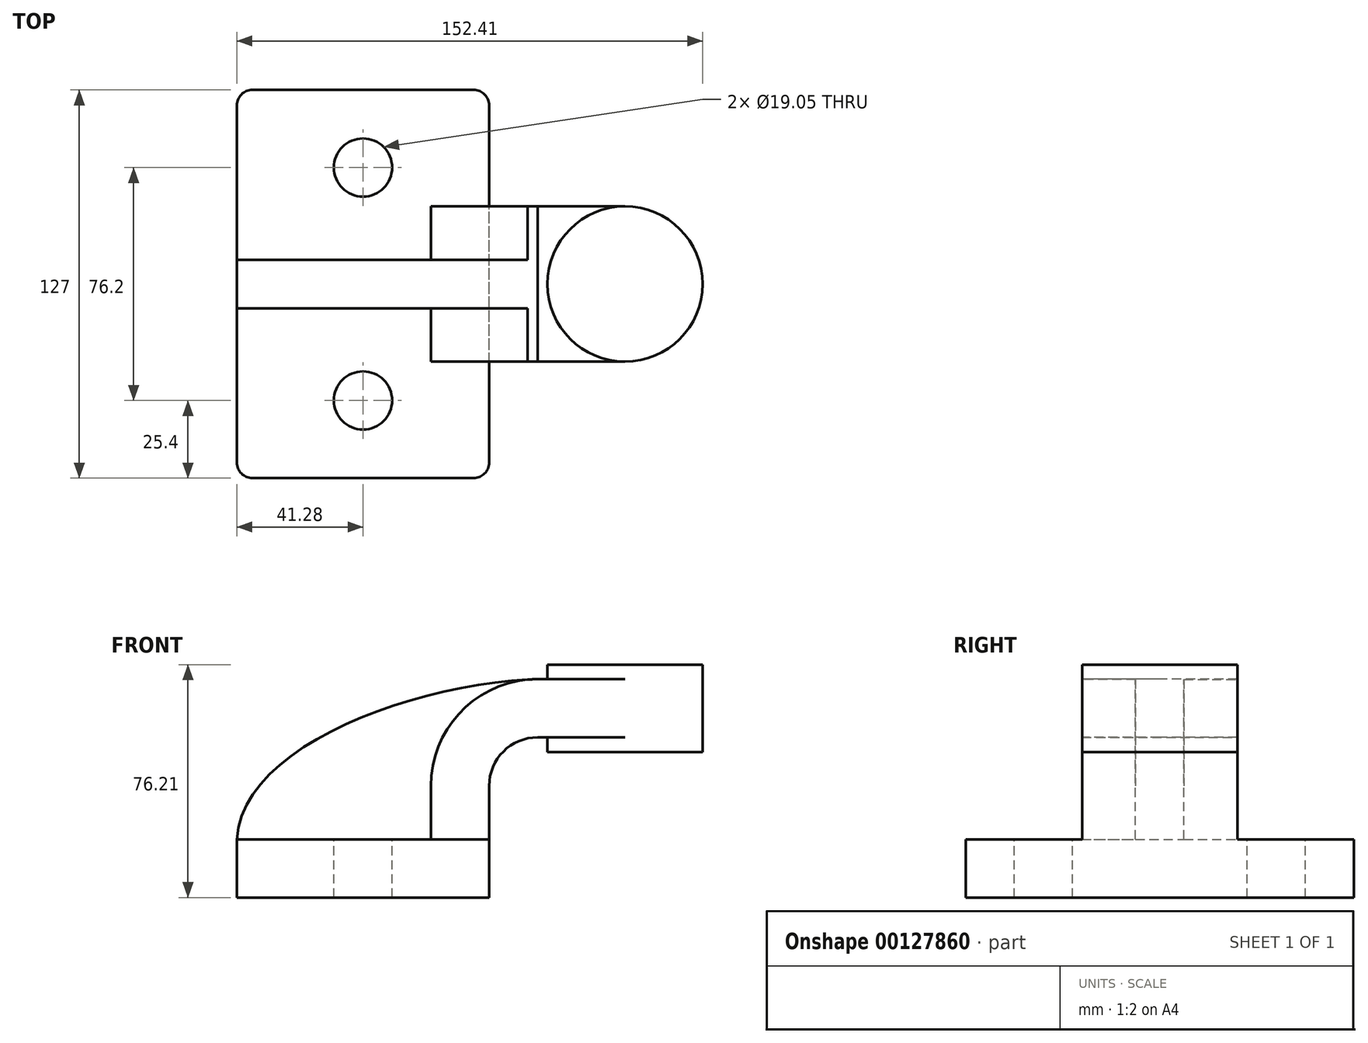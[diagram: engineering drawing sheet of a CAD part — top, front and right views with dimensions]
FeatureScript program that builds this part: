
annotation { "Feature Type Name" : "Feature", "Feature Type Description" : "" }
export const myFeature = defineFeature(function(context is Context, id is Id, definition is map)
    precondition{}
    {
        {
            var Q0;
            Q0=qCreatedBy(makeId("Front.planeOp"),FACE);
            var sketch = newSketch(context, id + "F0", { "sketchPlane" : qUnion([Q0])});
            skLineSegment(sketch, "E0.rect.bottom", {"start": v(-41.28, 9.52) * mm, "end": v(41.28, 9.52) * mm});
            skLineSegment(sketch, "E0.rect.top", {"start": v(-41.28, -9.52) * mm, "end": v(41.28, -9.52) * mm});
            skLineSegment(sketch, "E0.rect.left", {"start": v(-41.28, 9.52) * mm, "end": v(-41.28, -9.52) * mm});
            skLineSegment(sketch, "E0.rect.right", {"start": v(41.28, 9.52) * mm, "end": v(41.28, -9.52) * mm});
            skPoint(sketch, "E0.rect.middle", {"position": v(0, 0) * mm});
            skLineSegment(sketch, "E1", {"start": v(41.28, 9.52) * mm, "end": v(41.28, 27) * mm});
            skArc(sketch, "E2", {"start": v(41.28, 27) * mm, "mid": v(45.92, 38.23) * mm, "end": v(57.15, 42.88) * mm});
            skLineSegment(sketch, "E3", {"start": v(57.15, 42.88) * mm, "end": v(85.72, 42.88) * mm});
            skLineSegment(sketch, "E4.rect.bottom", {"start": v(60.32, 38.1) * mm, "end": v(111.12, 38.1) * mm});
            skLineSegment(sketch, "E4.rect.top", {"start": v(60.32, 66.68) * mm, "end": v(111.12, 66.68) * mm});
            skLineSegment(sketch, "E4.rect.left", {"start": v(60.32, 38.1) * mm, "end": v(60.32, 66.68) * mm});
            skLineSegment(sketch, "E4.rect.right", {"start": v(111.13, 38.1) * mm, "end": v(111.12, 66.68) * mm});
            skPoint(sketch, "E4.rect.middle", {"position": v(85.72, 52.39) * mm});
            skLineSegment(sketch, "E5.0", {"start": v(57.15, 61.93) * mm, "end": v(85.72, 61.93) * mm});
            skArc(sketch, "E5.1", {"start": v(22.23, 27) * mm, "mid": v(32.45, 51.7) * mm, "end": v(57.15, 61.93) * mm});
            skLineSegment(sketch, "E5.2", {"start": v(22.23, 9.52) * mm, "end": v(22.23, 27) * mm});
            skLineSegment(sketch, "E6", {"start": v(85.72, 38.1) * mm, "end": v(85.72, 66.68) * mm});
            skFitSpline(sketch, "E7", {"points": [v(-41.28, 9.53) * mm, v(57.15, 61.93) * mm], "startDerivative": vector(5.2, 92.34) * mm, "endDerivative": vector(120.92, 4.22) * mm});
            skSolve(sketch);
        }
        {
            var Q0;
            Q0=makeQuery(id+"F0.imprint","IMPRINT",FACE,{"disambiguationData":[TD([[makeQuery(id+"F0.imprint","IMPRINT",EDGE,{"derivedFrom":sQuery(id+"F0.wireOp",EDGE,"E0.rect.top")}),1.0]])]});
            extrude(context, id + "F1", {"entities" : qUnion([Q0]), "endBound" : BoundingType.SYMMETRIC, "depth" : 127 * mm});
        }
        {
            var Q0;
            {var subQ9=sQuery(id+"F0.wireOp",EDGE,"E1");Q0=makeQuery(id+"F0.imprint","IMPRINT",FACE,{"disambiguationData":[TD([[makeQuery(id+"F0.imprint","IMPRINT",EDGE,{"derivedFrom":subQ9}),1.0]])]});}
            var Q1;
            {var subQ0=sQuery(id+"F0.wireOp",EDGE,"E6");var subQ1=sQuery(id+"F0.wireOp",EDGE,"E3");var subQ2=makeQuery(id+"F0.imprint","INTERSECT",VERTEX,{"derivedFrom":[subQ1,subQ0]});Q1=makeQuery(id+"F0.imprint","IMPRINT",FACE,{"disambiguationData":[TD([[makeQuery(id+"F0.imprint","IMPRINT",EDGE,{"disambiguationData":[TD([[subQ2,1.0]])],"derivedFrom":subQ1}),1.0]])]});}
            extrude(context, id + "F2", {"entities" : qUnion([Q0, Q1]), "operationType" : NewBodyOperationType.ADD, "endBound" : BoundingType.SYMMETRIC, "depth" : 50.8 * mm});
        }
        {
            var Q0;
            {var subQ3=sQuery(id+"F0.wireOp",EDGE,"E5.2");Q0=makeQuery(id+"F0.imprint","IMPRINT",FACE,{"disambiguationData":[TD([[makeQuery(id+"F0.imprint","IMPRINT",EDGE,{"derivedFrom":subQ3}),1.0]])]});}
            extrude(context, id + "F3", {"entities" : qUnion([Q0]), "operationType" : NewBodyOperationType.ADD, "endBound" : BoundingType.SYMMETRIC, "depth" : 15.88 * mm});
        }
        {
            var Q0;
            {var subQ5=sQuery(id+"F0.wireOp",EDGE,"E4.rect.right");Q0=makeQuery(id+"F0.imprint","IMPRINT",FACE,{"disambiguationData":[TD([[makeQuery(id+"F0.imprint","IMPRINT",EDGE,{"derivedFrom":subQ5}),1.0]])]});}
            var Q1;
            Q1=sQuery(id+"F0.wireOp",EDGE,"E6");
            revolve(context, id + "F4", {"operationType" : NewBodyOperationType.ADD, "entities" : qUnion([Q0]), "axis" : qUnion([Q1]), "revolveType" : RevolveType.FULL});
        }
        {
            var Q0;
            Q0=makeQuery(id+"F1.opExtrude","CAP_EDGE",EDGE,{"disambiguationData":[OSD([sQuery(id+"F0.wireOp",EDGE,"E0.rect.right")])],"isStart":false});
            var Q1;
            Q1=makeQuery(id+"F1.opExtrude","CAP_EDGE",EDGE,{"disambiguationData":[OSD([sQuery(id+"F0.wireOp",EDGE,"E0.rect.left")])],"isStart":false});
            var Q2;
            Q2=makeQuery(id+"F1.opExtrude","CAP_EDGE",EDGE,{"disambiguationData":[OSD([sQuery(id+"F0.wireOp",EDGE,"E0.rect.right")])],"isStart":true});
            var Q3;
            Q3=makeQuery(id+"F1.opExtrude","CAP_EDGE",EDGE,{"disambiguationData":[OSD([sQuery(id+"F0.wireOp",EDGE,"E0.rect.left")])],"isStart":true});
            fillet(context, id + "F5", {"entities" : qUnion([Q0, Q1, Q2, Q3]), "radius" : 5.08 * mm, "tangentPropagation" : true, "allowEdgeOverflow" : false});
        }
        {
            var Q0;
            {var subQ4=sQuery(id+"F0.wireOp",EDGE,"E0.rect.bottom");var subQ5=sQuery(id+"F0.wireOp",EDGE,"E0.rect.right");var subQ6=sQuery(id+"F0.wireOp",EDGE,"E0.rect.left");Q0=makeQuery(id+"F3.boolean.opBoolean","SPLIT",FACE,{"disambiguationData":[TD([makeQuery(id+"F1.opExtrude","CAP_FACE",FACE,{"disambiguationData":[OSD([subQ4,sQuery(id+"F0.wireOp",EDGE,"E0.rect.top"),subQ6,subQ5])],"isStart":false})])],"derivedFrom":makeQuery(id+"F1.opExtrude","SWEPT_FACE",FACE,{"disambiguationData":[OSD([subQ4])]})});}
            var sketch = newSketch(context, id + "F6", { "sketchPlane" : qUnion([Q0])});
            skCircle(sketch, "E8", {"center": v(0, -38.1) * mm, "radius": 9.53 * mm});
            skCircle(sketch, "E9", {"center": v(0, 38.1) * mm, "radius": 9.53 * mm});
            skSolve(sketch);
        }
        {
            var Q0;
            Q0=makeQuery(id+"F6.imprint","IMPRINT",FACE,{"disambiguationData":[TD([[makeQuery(id+"F6.imprint","IMPRINT",EDGE,{"derivedFrom":sQuery(id+"F6.wireOp",EDGE,"E9")}),1.0]])]});
            var Q1;
            Q1=makeQuery(id+"F6.imprint","IMPRINT",FACE,{"disambiguationData":[TD([[makeQuery(id+"F6.imprint","IMPRINT",EDGE,{"derivedFrom":sQuery(id+"F6.wireOp",EDGE,"E8")}),1.0]])]});
            extrude(context, id + "F7", {"entities" : qUnion([Q0, Q1]), "operationType" : NewBodyOperationType.REMOVE, "endBound" : BoundingType.THROUGH_ALL, "oppositeDirection" : true, "depth" : 134.15 * mm});
        }
    });
